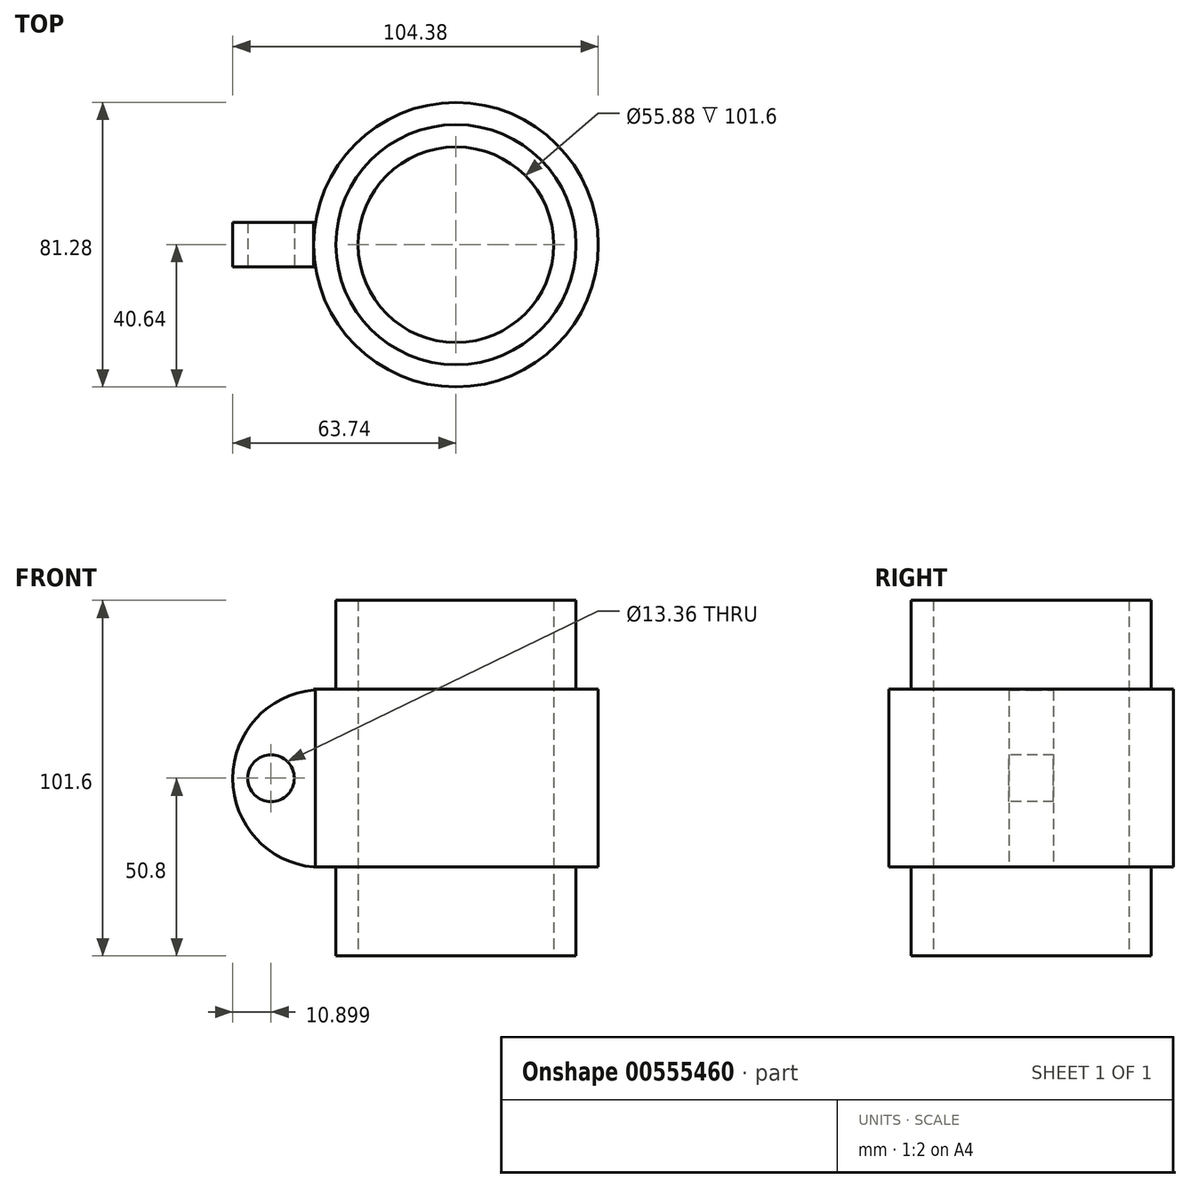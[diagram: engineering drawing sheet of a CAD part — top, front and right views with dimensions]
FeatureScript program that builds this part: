
annotation { "Feature Type Name" : "Feature", "Feature Type Description" : "" }
export const myFeature = defineFeature(function(context is Context, id is Id, definition is map)
    precondition{}
    {
        {
            var Q0;
            Q0=qCreatedBy(makeId("Front.planeOp"),FACE);
            var sketch = newSketch(context, id + "F0", { "sketchPlane" : qUnion([Q0])});
            skLineSegment(sketch, "E0.bottom", {"start": v(-27.94, 0) * mm, "end": v(-40.64, 0) * mm});
            skLineSegment(sketch, "E0.top", {"start": v(-27.94, 50.8) * mm, "end": v(-40.64, 50.8) * mm});
            skLineSegment(sketch, "E0.left", {"start": v(-27.94, 0) * mm, "end": v(-27.94, 50.8) * mm});
            skLineSegment(sketch, "E0.right", {"start": v(-40.64, 0) * mm, "end": v(-40.64, 50.8) * mm});
            skLineSegment(sketch, "E1", {"start": v(0, 0) * mm, "end": v(0, 38.6) * mm});
            skSolve(sketch);
        }
        {
            var Q0;
            Q0=makeQuery(id+"F0.imprint","IMPRINT",FACE,{"disambiguationData":[TD([[makeQuery(id+"F0.imprint","IMPRINT",EDGE,{"derivedFrom":sQuery(id+"F0.wireOp",EDGE,"E0.bottom")}),-1.0]])]});
            var Q1;
            Q1=sQuery(id+"F0.wireOp",EDGE,"E1");
            revolve(context, id + "F1", {"entities" : qUnion([Q0]), "axis" : qUnion([Q1]), "revolveType" : RevolveType.FULL});
        }
        {
            var Q0;
            Q0=qCreatedBy(makeId("Front.planeOp"),FACE);
            var sketch = newSketch(context, id + "F2", { "sketchPlane" : qUnion([Q0])});
            skArc(sketch, "E2", {"start": v(-40.64, 50.6) * mm, "mid": v(-63.74, 25.3) * mm, "end": v(-40.64, 0) * mm});
            skLineSegment(sketch, "E3", {"start": v(-40.64, 50.6) * mm, "end": v(-40.64, 0) * mm});
            skLineSegment(sketch, "E4.bottom", {"start": v(-40.64, 50.6) * mm, "end": v(-35.56, 50.6) * mm});
            skLineSegment(sketch, "E4.top", {"start": v(-40.64, 0) * mm, "end": v(-35.56, 0) * mm});
            skLineSegment(sketch, "E4.right", {"start": v(-35.56, 50.6) * mm, "end": v(-35.56, 0) * mm});
            skSolve(sketch);
        }
        {
            var Q0;
            Q0=qSketchRegion(id+"F2",true);
            extrude(context, id + "F3", {"entities" : qUnion([Q0]), "operationType" : NewBodyOperationType.ADD, "depth" : 6.35 * mm, "offsetDistance" : 25.4 * mm, "hasSecondDirection" : true, "secondDirectionOppositeDirection" : true, "secondDirectionDepth" : 6.35 * mm});
        }
        {
            var Q0;
            Q0=makeQuery(id+"F3.opExtrude","CAP_FACE",FACE,{"disambiguationData":[OSD([sQuery(id+"F2.wireOp",EDGE,"E2"),sQuery(id+"F2.wireOp",EDGE,"E4.bottom"),sQuery(id+"F2.wireOp",EDGE,"E4.top"),sQuery(id+"F2.wireOp",EDGE,"E4.right")])],"isStart":false});
            var sketch = newSketch(context, id + "F4", { "sketchPlane" : qUnion([Q0])});
            skCircle(sketch, "E5", {"center": v(-52.84, 25.4) * mm, "radius": 6.68 * mm});
            skSolve(sketch);
        }
        {
            var Q0;
            Q0=makeQuery(id+"F4.imprint","IMPRINT",FACE,{"disambiguationData":[TD([[makeQuery(id+"F4.imprint","IMPRINT",EDGE,{"derivedFrom":sQuery(id+"F4.wireOp",EDGE,"E5")}),1.0]])]});
            extrude(context, id + "F5", {"entities" : qUnion([Q0]), "operationType" : NewBodyOperationType.REMOVE, "oppositeDirection" : true, "depth" : 25.4 * mm, "offsetDistance" : 25.4 * mm});
        }
        {
            var Q0;
            Q0=qCreatedBy(makeId("Front.planeOp"),FACE);
            var sketch = newSketch(context, id + "F6", { "sketchPlane" : qUnion([Q0])});
            skLineSegment(sketch, "E6", {"start": v(0, 0) * mm, "end": v(0, 69.09) * mm});
            skSolve(sketch);
        }
        {
            var Q0;
            Q0=qCreatedBy(makeId("Front.planeOp"),FACE);
            var sketch = newSketch(context, id + "F7", { "sketchPlane" : qUnion([Q0])});
            skLineSegment(sketch, "E7.bottom", {"start": v(-27.94, 76.2) * mm, "end": v(-34.3, 76.2) * mm});
            skLineSegment(sketch, "E7.top", {"start": v(-27.94, -25.4) * mm, "end": v(-34.3, -25.4) * mm});
            skLineSegment(sketch, "E7.left", {"start": v(-27.94, 76.2) * mm, "end": v(-27.94, -25.4) * mm});
            skLineSegment(sketch, "E7.right", {"start": v(-34.3, 76.2) * mm, "end": v(-34.3, -25.4) * mm});
            skLineSegment(sketch, "E8", {"start": v(0, 0) * mm, "end": v(0, 147.64) * mm});
            skSolve(sketch);
        }
        {
            var Q0;
            Q0=makeQuery(id+"F7.imprint","IMPRINT",FACE,{"disambiguationData":[TD([[makeQuery(id+"F7.imprint","IMPRINT",EDGE,{"derivedFrom":sQuery(id+"F7.wireOp",EDGE,"E7.bottom")}),1.0]])]});
            var Q1;
            Q1=sQuery(id+"F7.wireOp",EDGE,"E8");
            revolve(context, id + "F8", {"operationType" : NewBodyOperationType.ADD, "entities" : qUnion([Q0]), "axis" : qUnion([Q1]), "revolveType" : RevolveType.FULL});
        }
    });
